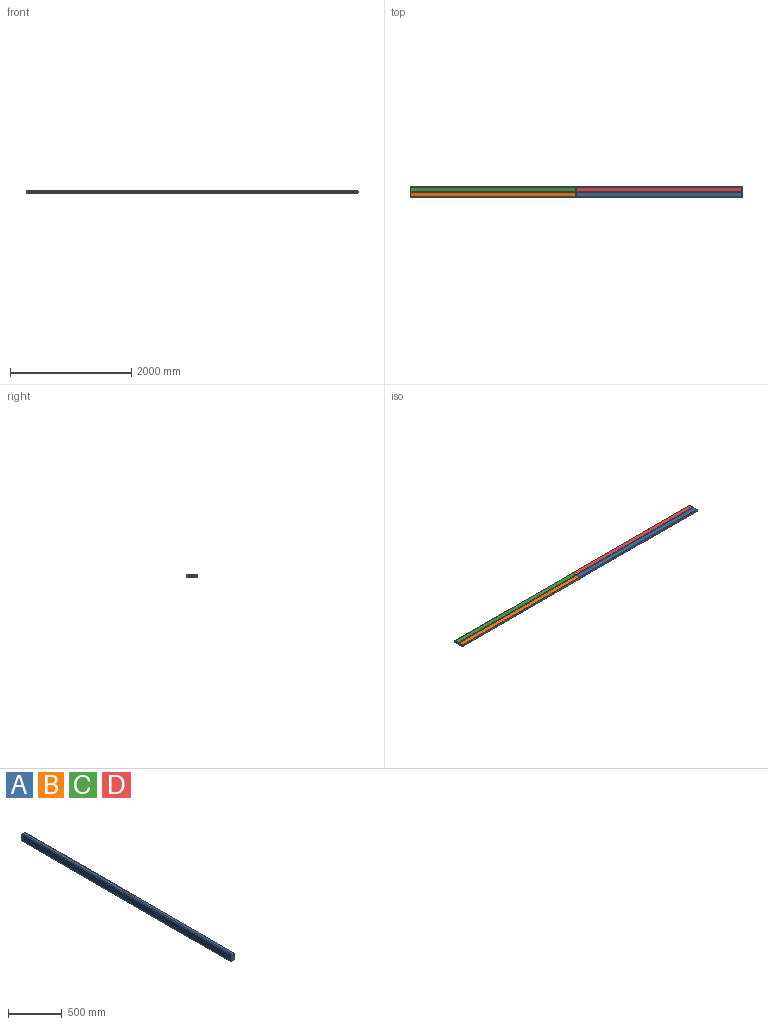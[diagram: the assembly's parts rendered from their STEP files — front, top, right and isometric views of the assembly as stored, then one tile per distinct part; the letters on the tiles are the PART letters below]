
ASSEMBLY  parts=4 mates=3
PART A: 26 faces, bbox 39.1x2743.2x89.9 mm
  f0: plane 2738.12x76.2mm, normal (-1,0,0), area 208644.7mm2, adj f6,f9,f13,f21
  f1: plane 2738.12x25.4mm, normal (0,0,-1), area 69548.2mm2, adj f6,f7,f10,f18
  f2: plane 2738.12x76.2mm, normal (1,0,0), area 208644.7mm2, adj f7,f8,f14,f22
  f3: plane 2738.12x25.4mm, normal (0,0,1), area 69548.2mm2, adj f8,f9,f17,f25
  f4: plane 83.82x33.02mm, normal (0,-1,0), area 2755.3mm2, adj f10,f11,f12,f13,f14,f15,f16,f17
  f5: plane 83.82x33.02mm, normal (0,1,0), area 2755.3mm2, adj f18,f19,f20,f21,f22,f23,f24,f25
  f6: cylinder r=6.35mm len=2738.12mm, axis (0,-1,0), area 27311.5mm2, adj f0,f1,f11,f19
  f7: cylinder r=6.35mm len=2738.12mm, axis (0,1,0), area 27311.5mm2, adj f1,f2,f12,f20
  f8: cylinder r=6.35mm len=2738.12mm, axis (0,-1,0), area 27311.5mm2, adj f2,f3,f16,f24
  f9: cylinder r=6.35mm len=2738.12mm, axis (0,1,0), area 27311.5mm2, adj f0,f3,f15,f23
  f10: cylinder r=2.54mm len=25.4mm, axis (-1,0,0), area 101.3mm2, adj f1,f4,f11,f12
  f11: torus R=3.81mm, axis (0,-1,0), area 34mm2, adj f4,f6,f10,f13
  f12: torus R=3.81mm, axis (0,-1,0), area 34mm2, adj f4,f7,f10,f14
  f13: cylinder r=2.54mm len=76.2mm, axis (0,0,1), area 304mm2, adj f0,f4,f11,f15
  f14: cylinder r=2.54mm len=76.2mm, axis (0,0,-1), area 304mm2, adj f2,f4,f12,f16
  f15: torus R=3.81mm, axis (0,-1,0), area 34mm2, adj f4,f9,f13,f17
  f16: torus R=3.81mm, axis (0,-1,0), area 34mm2, adj f4,f8,f14,f17
  f17: cylinder r=2.54mm len=25.4mm, axis (1,0,0), area 101.3mm2, adj f3,f4,f15,f16
  f18: cylinder r=2.54mm len=25.4mm, axis (1,0,0), area 101.3mm2, adj f1,f5,f19,f20
  f19: torus R=3.81mm, axis (0,-1,0), area 34mm2, adj f5,f6,f18,f21
  f20: torus R=3.81mm, axis (0,-1,0), area 34mm2, adj f5,f7,f18,f22
  f21: cylinder r=2.54mm len=76.2mm, axis (0,0,-1), area 304mm2, adj f0,f5,f19,f23
  f22: cylinder r=2.54mm len=76.2mm, axis (0,0,1), area 304mm2, adj f2,f5,f20,f24
  f23: torus R=3.81mm, axis (0,-1,0), area 34mm2, adj f5,f9,f21,f25
  f24: torus R=3.81mm, axis (0,-1,0), area 34mm2, adj f5,f8,f22,f25
  f25: cylinder r=2.54mm len=25.4mm, axis (-1,0,0), area 101.3mm2, adj f3,f5,f23,f24
PART B: same geometry as A
PART C: same geometry as A
PART D: same geometry as A
PLACE A rot(axis=(-0.58,-0.58,-0.58),120deg) t=(4143.63,-318.93,-1141.16)mm
PLACE B rot(axis=(-0.58,-0.58,-0.58),120deg) t=(1400.43,-318.93,-1141.16)mm
PLACE C rot(axis=(0.58,0.58,-0.58),120deg) t=(1400.43,-141.13,-1103.06)mm
PLACE D rot(axis=(0.58,0.58,-0.58),120deg) t=(4143.63,-141.13,-1103.06)mm
MATE fastened C.f3 <-> B.f3  axis (0,-1,0) through (28.83,-230.03,-1122.11)mm
MATE fastened A.f4 <-> B.f5  axis (-1,0,0) through (1400.43,-274.48,-1122.11)mm
MATE fastened C.f5 <-> D.f4  axis (1,0,0) through (1400.43,-185.58,-1122.11)mm
